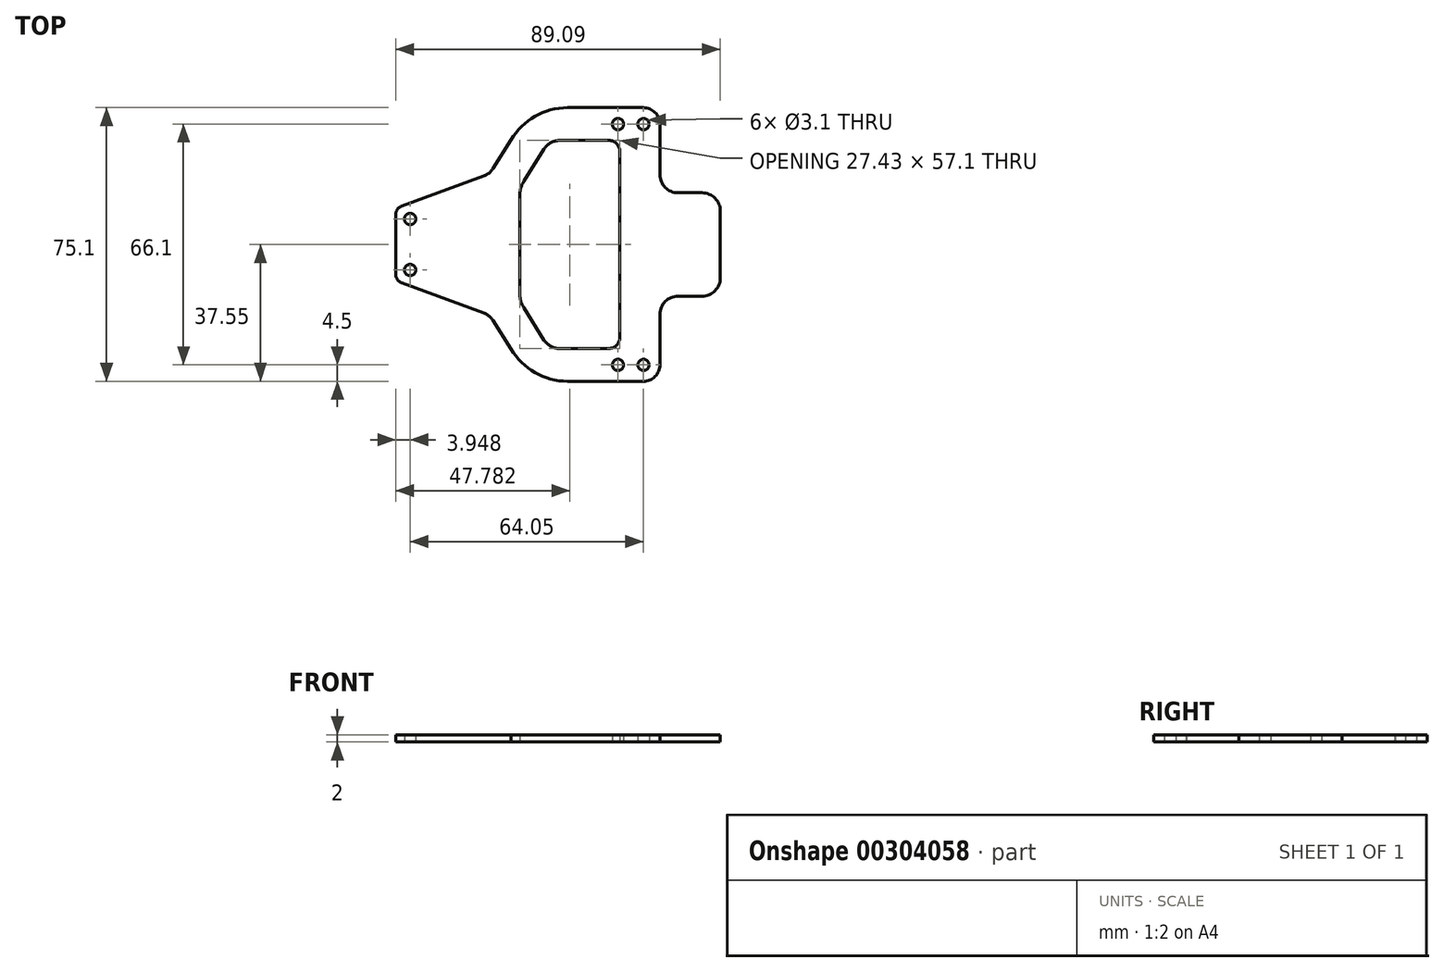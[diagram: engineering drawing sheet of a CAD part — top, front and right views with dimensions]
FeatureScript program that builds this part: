
annotation { "Feature Type Name" : "Feature", "Feature Type Description" : "" }
export const myFeature = defineFeature(function(context is Context, id is Id, definition is map)
    precondition{}
    {
        {
            var Q0;
            Q0=qCreatedBy(makeId("Top.planeOp"),FACE);
            var sketch = newSketch(context, id + "F0", { "sketchPlane" : qUnion([Q0])});
            skLineSegment(sketch, "E0.bottom", {"start": v(0, 0) * mm, "end": v(0, 0) * mm});
            skLineSegment(sketch, "E0.top", {"start": v(0, 0) * mm, "end": v(0, 0) * mm});
            skLineSegment(sketch, "E0.left", {"start": v(0, 0) * mm, "end": v(0, 0) * mm});
            skLineSegment(sketch, "E0.right", {"start": v(0, 0) * mm, "end": v(0, 0) * mm});
            skPoint(sketch, "E1.middle", {"position": v(0, 0) * mm});
            skLineSegment(sketch, "E2.left", {"start": v(24.32, 33.05) * mm, "end": v(24.32, 33.05) * mm});
            skArc(sketch, "E3.filletArc", {"start": v(24.32, 33.05) * mm, "mid": v(23, 36.23) * mm, "end": v(19.82, 37.55) * mm});
            skCircle(sketch, "E4", {"center": v(19.82, 33.05) * mm, "radius": 1.55 * mm});
            skCircle(sketch, "E5", {"center": v(12.82, 33.05) * mm, "radius": 1.55 * mm});
            skCircle(sketch, "E6", {"center": v(-44.23, 7) * mm, "radius": 1.55 * mm});
            skArc(sketch, "E7.MirrorCS", {"start": v(24.32, -33.05) * mm, "mid": v(23, -36.23) * mm, "end": v(19.82, -37.55) * mm});
            skCircle(sketch, "E8.MirrorC", {"center": v(19.82, -33.05) * mm, "radius": 1.55 * mm});
            skCircle(sketch, "E9.MirrorC", {"center": v(12.82, -33.05) * mm, "radius": 1.55 * mm});
            skPoint(sketch, "E10.visualSharp", {"position": v(-22.39, 19.4) * mm});
            skCircle(sketch, "E11", {"center": v(-44.23, -7) * mm, "radius": 1.55 * mm});
            skPoint(sketch, "E12.newPointA", {"position": v(-48.18, 9.16) * mm});
            skArc(sketch, "E12.filletArc", {"start": v(-46.54, 10.55) * mm, "mid": v(-47.73, 9.63) * mm, "end": v(-48.18, 8.2) * mm});
            skArc(sketch, "E13.MirrorCS", {"start": v(-46.54, -10.55) * mm, "mid": v(-47.73, -9.63) * mm, "end": v(-48.18, -8.2) * mm});
            skLineSegment(sketch, "E14", {"start": v(-48.18, 8.2) * mm, "end": v(-48.18, -8.2) * mm});
            skLineSegment(sketch, "E15", {"start": v(-1.04, 37.55) * mm, "end": v(19.82, 37.55) * mm});
            skArc(sketch, "E16.filletArc", {"start": v(-1.04, 37.55) * mm, "mid": v(-9.97, 35.18) * mm, "end": v(-16.55, 28.69) * mm});
            skLineSegment(sketch, "E17", {"start": v(-46.54, 10.55) * mm, "end": v(-24, 18.8) * mm});
            skLineSegment(sketch, "E18", {"start": v(-16.55, 28.69) * mm, "end": v(-21.48, 20.84) * mm});
            skArc(sketch, "E19.filletArc", {"start": v(-24, 18.8) * mm, "mid": v(-22.57, 19.62) * mm, "end": v(-21.48, 20.84) * mm});
            skLineSegment(sketch, "E20.MirrorCS", {"start": v(-46.54, -10.55) * mm, "end": v(-24, -18.8) * mm});
            skLineSegment(sketch, "E21.MirrorCS", {"start": v(-16.55, -28.69) * mm, "end": v(-21.48, -20.84) * mm});
            skArc(sketch, "E22.MirrorCS", {"start": v(-1.04, -37.55) * mm, "mid": v(-9.97, -35.18) * mm, "end": v(-16.55, -28.69) * mm});
            skLineSegment(sketch, "E23.MirrorCS", {"start": v(-1.04, -37.55) * mm, "end": v(19.82, -37.55) * mm});
            skArc(sketch, "E24.MirrorCS", {"start": v(-24, -18.8) * mm, "mid": v(-22.57, -19.62) * mm, "end": v(-21.48, -20.84) * mm});
            skLineSegment(sketch, "E25", {"start": v(-7.47, 26.21) * mm, "end": v(-13.04, 17.36) * mm});
            skArc(sketch, "E26.filletArc", {"start": v(-3.24, 28.55) * mm, "mid": v(-5.66, 27.93) * mm, "end": v(-7.47, 26.21) * mm});
            skLineSegment(sketch, "E27.MirrorCS", {"start": v(-7.47, -26.21) * mm, "end": v(-13.04, -17.36) * mm});
            skArc(sketch, "E28.MirrorCS", {"start": v(-3.24, -28.55) * mm, "mid": v(-5.66, -27.93) * mm, "end": v(-7.47, -26.21) * mm});
            skLineSegment(sketch, "E29", {"start": v(-14.11, 13.63) * mm, "end": v(-14.11, -13.63) * mm});
            skPoint(sketch, "E30.visualSharp", {"position": v(-14.11, 15.65) * mm});
            skArc(sketch, "E30.filletArc", {"start": v(-13.04, 17.36) * mm, "mid": v(-13.84, 15.57) * mm, "end": v(-14.11, 13.63) * mm});
            skPoint(sketch, "E31.visualSharp", {"position": v(-14.11, -15.65) * mm});
            skArc(sketch, "E31.filletArc", {"start": v(-14.11, -13.63) * mm, "mid": v(-13.84, -15.57) * mm, "end": v(-13.04, -17.36) * mm});
            skLineSegment(sketch, "E32", {"start": v(13.32, 25.55) * mm, "end": v(13.32, -25.55) * mm});
            skLineSegment(sketch, "E33", {"start": v(24.32, -19.18) * mm, "end": v(24.32, -33.05) * mm});
            skArc(sketch, "E34.filletArc", {"start": v(13.32, 25.55) * mm, "mid": v(12.44, 27.67) * mm, "end": v(10.32, 28.55) * mm});
            skArc(sketch, "E35.filletArc", {"start": v(10.32, -28.55) * mm, "mid": v(12.44, -27.67) * mm, "end": v(13.32, -25.55) * mm});
            skLineSegment(sketch, "E36", {"start": v(-3.24, 28.55) * mm, "end": v(10.32, 28.55) * mm});
            skLineSegment(sketch, "E37", {"start": v(-3.24, -28.55) * mm, "end": v(10.32, -28.55) * mm});
            skLineSegment(sketch, "E38", {"start": v(29.32, 14.18) * mm, "end": v(35.91, 14.18) * mm});
            skLineSegment(sketch, "E39", {"start": v(40.91, 9.18) * mm, "end": v(40.91, 0) * mm});
            skLineSegment(sketch, "E40.MirrorCS", {"start": v(29.32, -14.18) * mm, "end": v(35.91, -14.18) * mm});
            skLineSegment(sketch, "E41.MirrorCS", {"start": v(40.91, -9.18) * mm, "end": v(40.91, 0) * mm});
            skPoint(sketch, "E42.visualSharp", {"position": v(40.91, 14.18) * mm});
            skArc(sketch, "E42.filletArc", {"start": v(40.91, 9.18) * mm, "mid": v(39.45, 12.72) * mm, "end": v(35.91, 14.18) * mm});
            skPoint(sketch, "E43.visualSharp", {"position": v(40.91, -14.18) * mm});
            skArc(sketch, "E43.filletArc", {"start": v(35.91, -14.18) * mm, "mid": v(39.45, -12.72) * mm, "end": v(40.91, -9.18) * mm});
            skPoint(sketch, "E44.newPointB", {"position": v(24.32, -14.18) * mm});
            skArc(sketch, "E44.filletArc", {"start": v(29.32, -14.18) * mm, "mid": v(25.78, -15.65) * mm, "end": v(24.32, -19.18) * mm});
            skLineSegment(sketch, "E45", {"start": v(24.32, 33.05) * mm, "end": v(24.32, 19.18) * mm});
            skPoint(sketch, "E46.visualSharp", {"position": v(24.32, 14.18) * mm});
            skArc(sketch, "E46.filletArc", {"start": v(24.32, 19.18) * mm, "mid": v(25.78, 15.65) * mm, "end": v(29.32, 14.18) * mm});
            skSolve(sketch);
        }
        {
            var Q0;
            Q0 = qSketchRegion(id + "F0", true);
            extrude(context, id + "F1", {"entities" : qUnion([Q0]), "depth" : 2 * mm});
        }
    });
